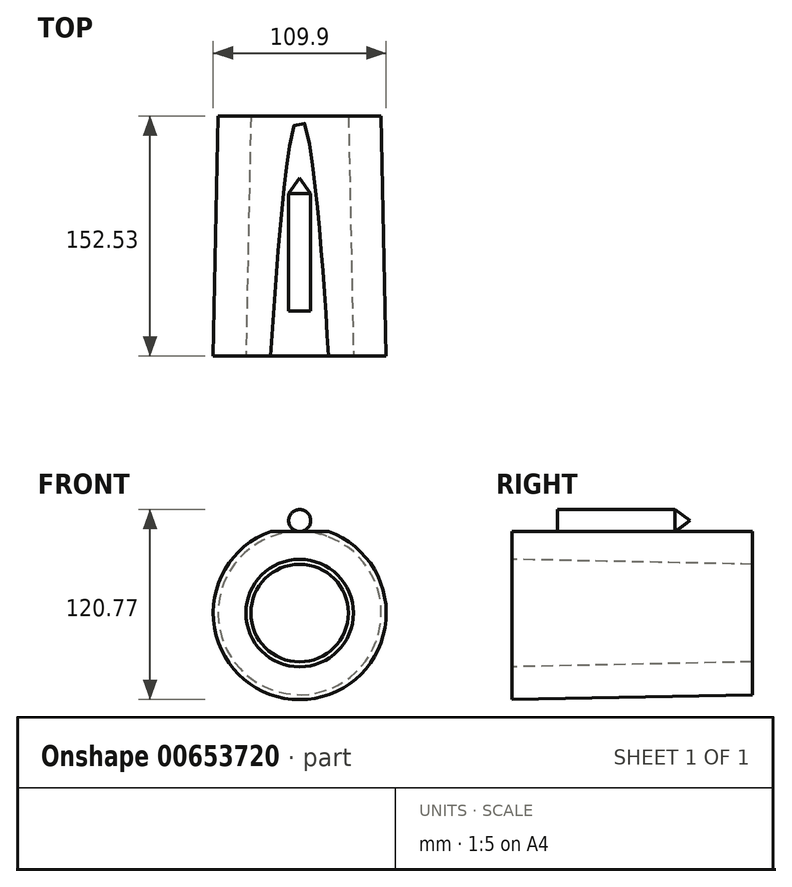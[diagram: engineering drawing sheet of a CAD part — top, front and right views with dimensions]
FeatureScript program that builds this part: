
annotation { "Feature Type Name" : "Feature", "Feature Type Description" : "" }
export const myFeature = defineFeature(function(context is Context, id is Id, definition is map)
    precondition{}
    {
        {
            var Q0;
            Q0=qCreatedBy(makeId("Right.planeOp"),FACE);
            var sketch = newSketch(context, id + "F0", { "sketchPlane" : qUnion([Q0])});
            skLineSegment(sketch, "E0", {"start": v(-76.32, -34.12) * mm, "end": v(76.2, -30.96) * mm});
            skLineSegment(sketch, "E1", {"start": v(-0.2, 0.04) * mm, "end": v(-52.14, 0.04) * mm});
            skLineSegment(sketch, "E2", {"start": v(-76.32, -54.9) * mm, "end": v(76.2, -51.75) * mm});
            skLineSegment(sketch, "E3", {"start": v(-76.32, -34.12) * mm, "end": v(-76.32, -54.9) * mm});
            skLineSegment(sketch, "E4", {"start": v(76.2, -30.96) * mm, "end": v(76.2, -51.75) * mm});
            skSolve(sketch);
        }
        {
            var Q0;
            Q0=makeQuery(id+"F0.imprint","IMPRINT",FACE,{"disambiguationData":[TD([[makeQuery(id+"F0.imprint","IMPRINT",EDGE,{"derivedFrom":sQuery(id+"F0.wireOp",EDGE,"E0")}),-1.0]])]});
            var Q1;
            Q1=sQuery(id+"F0.wireOp",EDGE,"E1");
            revolve(context, id + "F1", {"entities" : qUnion([Q0]), "axis" : qUnion([Q1]), "revolveType" : RevolveType.FULL});
        }
        {
            var Q0;
            Q0=qCreatedBy(makeId("Right.planeOp"),FACE);
            var sketch = newSketch(context, id + "F2", { "sketchPlane" : qUnion([Q0])});
            skLineSegment(sketch, "E5.bottom", {"start": v(76.2, 51.84) * mm, "end": v(-77.64, 51.84) * mm});
            skLineSegment(sketch, "E5.left", {"start": v(76.2, 51.84) * mm, "end": v(76.2, 58.85) * mm});
            skLineSegment(sketch, "E5.right", {"start": v(-77.64, 51.84) * mm, "end": v(-77.64, 58.85) * mm});
            skLineSegment(sketch, "E6", {"start": v(76.2, 58.85) * mm, "end": v(-77.64, 58.85) * mm});
            skLineSegment(sketch, "E7", {"start": v(36.64, 58.85) * mm, "end": v(27.02, 65.86) * mm});
            skLineSegment(sketch, "E8", {"start": v(27.02, 65.86) * mm, "end": v(-47.6, 65.86) * mm});
            skLineSegment(sketch, "E9", {"start": v(-47.6, 65.86) * mm, "end": v(-47.6, 58.85) * mm});
            skLineSegment(sketch, "E10", {"start": v(27.02, 65.86) * mm, "end": v(27.02, 58.85) * mm});
            skSolve(sketch);
        }
        {
            var Q0;
            Q0=makeQuery(id+"F2.imprint","IMPRINT",FACE,{"disambiguationData":[TD([[makeQuery(id+"F2.imprint","IMPRINT",EDGE,{"derivedFrom":sQuery(id+"F2.wireOp",EDGE,"E5.bottom")}),-1.0]])]});
            extrude(context, id + "F3", {"entities" : qUnion([Q0]), "operationType" : NewBodyOperationType.REMOVE, "oppositeDirection" : true, "depth" : 114.55 * mm, "offsetDistance" : 25.4 * mm, "hasSecondDirection" : true, "secondDirectionOppositeDirection" : false, "secondDirectionDepth" : 105.66 * mm});
        }
        {
            var Q0;
            Q0=makeQuery(id+"F2.imprint","IMPRINT",FACE,{"disambiguationData":[TD([[makeQuery(id+"F2.imprint","IMPRINT",EDGE,{"derivedFrom":sQuery(id+"F2.wireOp",EDGE,"E8")}),1.0]])]});
            var Q1;
            Q1=sQuery(id+"F2.wireOp",EDGE,"E6");
            revolve(context, id + "F4", {"operationType" : NewBodyOperationType.ADD, "entities" : qUnion([Q0]), "axis" : qUnion([Q1]), "revolveType" : RevolveType.FULL});
        }
        {
            var Q0;
            {var subQ0=sQuery(id+"F2.wireOp",EDGE,"E7");Q0=makeQuery(id+"F2.imprint","IMPRINT",FACE,{"disambiguationData":[TD([[makeQuery(id+"F2.imprint","IMPRINT",EDGE,{"derivedFrom":subQ0}),1.0]])]});}
            var Q1;
            Q1=sQuery(id+"F2.wireOp",EDGE,"E6");
            revolve(context, id + "F5", {"operationType" : NewBodyOperationType.ADD, "entities" : qUnion([Q0]), "axis" : qUnion([Q1]), "revolveType" : RevolveType.FULL});
        }
    });
